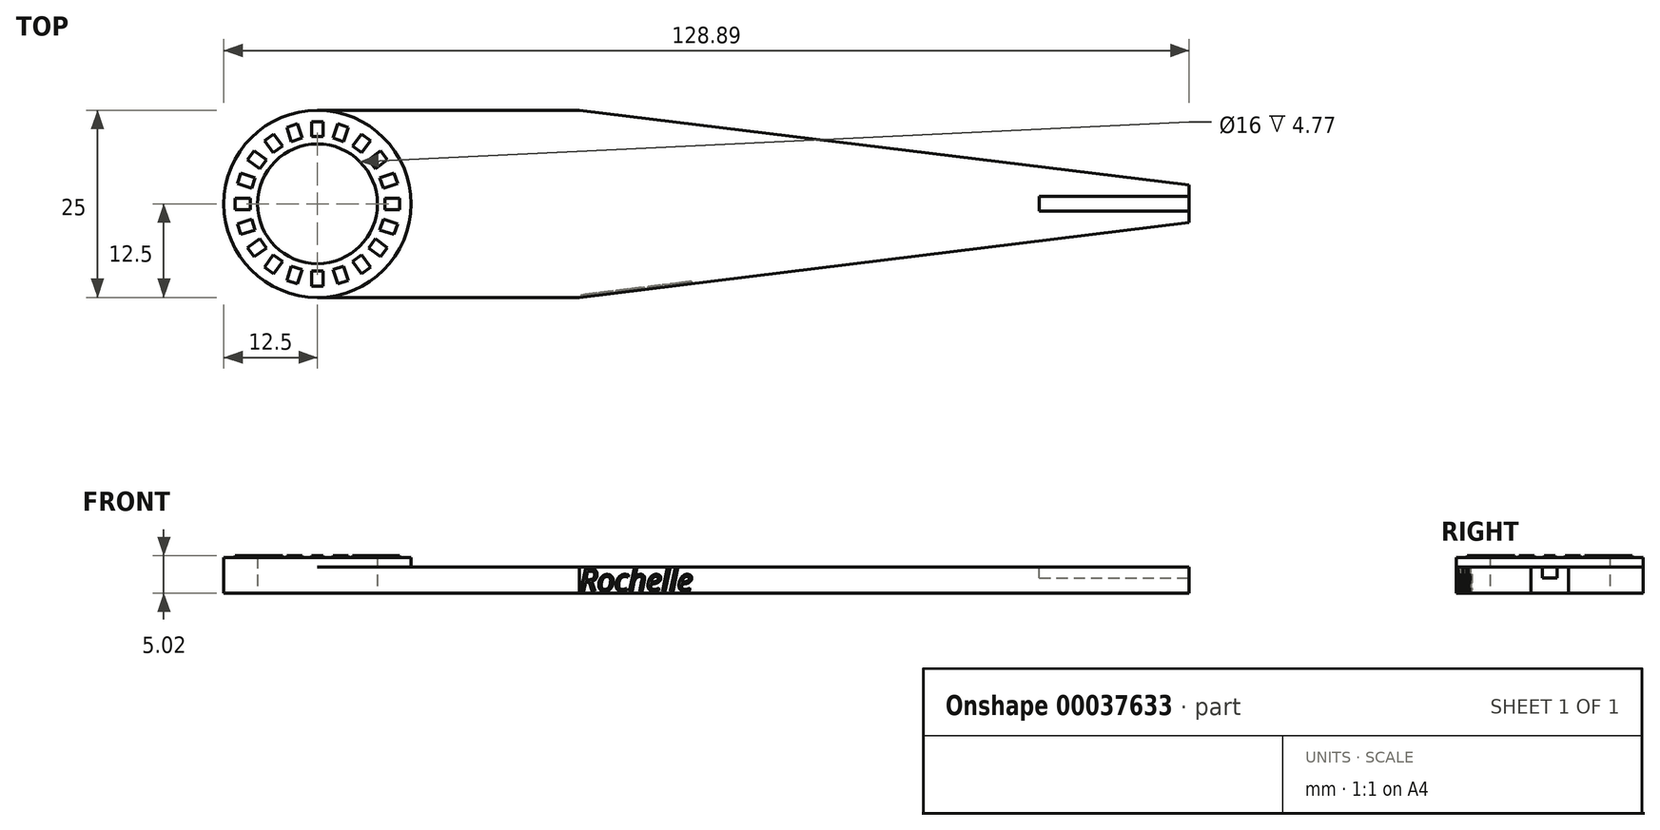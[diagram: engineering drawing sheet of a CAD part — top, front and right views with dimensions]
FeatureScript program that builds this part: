
annotation { "Feature Type Name" : "Feature", "Feature Type Description" : "" }
export const myFeature = defineFeature(function(context is Context, id is Id, definition is map)
    precondition{}
    {
        {
            var Q0;
            Q0=qCreatedBy(makeId("Top.planeOp"),FACE);
            var sketch = newSketch(context, id + "F0", { "sketchPlane" : qUnion([Q0])});
            skCircle(sketch, "E0", {"center": v(0, 0) * mm, "radius": 8 * mm});
            skCircle(sketch, "E1", {"center": v(0, 0) * mm, "radius": 12.5 * mm});
            skLineSegment(sketch, "E2", {"start": v(0, 12.5) * mm, "end": v(35, 12.5) * mm});
            skPoint(sketch, "E3", {"position": v(0, 12.5) * mm});
            skLineSegment(sketch, "E4", {"start": v(0, 0) * mm, "end": v(34.23, 0) * mm, "construction": true});
            skLineSegment(sketch, "E5.MirrorCS", {"start": v(0, -12.5) * mm, "end": v(35, -12.5) * mm});
            skLineSegment(sketch, "E6", {"start": v(35, 12.5) * mm, "end": v(74.55, 12.5) * mm, "construction": true});
            skLineSegment(sketch, "E7", {"start": v(35, 12.5) * mm, "end": v(116.39, 2.5) * mm});
            skLineSegment(sketch, "E8.MirrorCS", {"start": v(35, -12.5) * mm, "end": v(116.39, -2.5) * mm});
            skLineSegment(sketch, "E9", {"start": v(116.39, 2.5) * mm, "end": v(116.39, -2.5) * mm});
            skSolve(sketch);
        }
        {
            var Q0;
            Q0 = qSketchRegion(id + "F0", true);
            extrude(context, id + "F1", {"entities" : qUnion([Q0]), "depth" : 3.5 * mm});
        }
        {
            var Q0;
            Q0=makeQuery(id+"F1.opExtrude","CAP_FACE",FACE,{"disambiguationData":[OSD([sQuery(id+"F0.wireOp",EDGE,"E0"),sQuery(id+"F0.wireOp",EDGE,"E1"),sQuery(id+"F0.wireOp",EDGE,"E2"),sQuery(id+"F0.wireOp",EDGE,"E5.MirrorCS"),sQuery(id+"F0.wireOp",EDGE,"E7"),sQuery(id+"F0.wireOp",EDGE,"E8.MirrorCS"),sQuery(id+"F0.wireOp",EDGE,"E9")])],"isStart":false});
            var sketch = newSketch(context, id + "F2", { "sketchPlane" : qUnion([Q0])});
            skCircle(sketch, "E10", {"center": v(0, 0) * mm, "radius": 12.5 * mm});
            skCircle(sketch, "E11", {"center": v(0, 0) * mm, "radius": 8 * mm});
            skSolve(sketch);
        }
        {
            var Q0;
            Q0=makeQuery(id+"F2.imprint","IMPRINT",FACE,{"disambiguationData":[TD([[makeQuery(id+"F2.imprint","IMPRINT",EDGE,{"derivedFrom":sQuery(id+"F2.wireOp",EDGE,"E11")}),-1.0]])]});
            extrude(context, id + "F3", {"entities" : qUnion([Q0]), "operationType" : NewBodyOperationType.ADD, "depth" : 1.27 * mm});
        }
        {
            var Q0;
            Q0=makeQuery(id+"F3.opExtrude","CAP_FACE",FACE,{"disambiguationData":[OSD([sQuery(id+"F2.wireOp",EDGE,"E10"),sQuery(id+"F2.wireOp",EDGE,"E11")])],"isStart":false});
            var sketch = newSketch(context, id + "F4", { "sketchPlane" : qUnion([Q0])});
            skLineSegment(sketch, "E12.rect.bottom", {"start": v(0.75, 9) * mm, "end": v(-0.75, 9) * mm});
            skLineSegment(sketch, "E12.rect.top", {"start": v(0.75, 11) * mm, "end": v(-0.75, 11) * mm});
            skLineSegment(sketch, "E12.rect.left", {"start": v(0.75, 9) * mm, "end": v(0.75, 11) * mm});
            skLineSegment(sketch, "E12.rect.right", {"start": v(-0.75, 9) * mm, "end": v(-0.75, 11) * mm});
            skPoint(sketch, "E12.rect.middle", {"position": v(0, 10) * mm});
            skPoint(sketch, "E13", {"position": v(0, 8) * mm});
            skLineSegment(sketch, "E14.1.0", {"start": v(-2.69, 10.7) * mm, "end": v(-4.11, 10.23) * mm});
            skLineSegment(sketch, "E14.1.1", {"start": v(-2.07, 8.8) * mm, "end": v(-3.5, 8.33) * mm});
            skLineSegment(sketch, "E14.1.2", {"start": v(-3.5, 8.33) * mm, "end": v(-4.11, 10.23) * mm});
            skLineSegment(sketch, "E14.1.3", {"start": v(-2.07, 8.8) * mm, "end": v(-2.69, 10.7) * mm});
            skLineSegment(sketch, "E14.2.0", {"start": v(-5.86, 9.34) * mm, "end": v(-7.07, 8.46) * mm});
            skLineSegment(sketch, "E14.2.1", {"start": v(-4.68, 7.72) * mm, "end": v(-5.9, 6.84) * mm});
            skLineSegment(sketch, "E14.2.2", {"start": v(-5.9, 6.84) * mm, "end": v(-7.07, 8.46) * mm});
            skLineSegment(sketch, "E14.2.3", {"start": v(-4.68, 7.72) * mm, "end": v(-5.86, 9.34) * mm});
            skLineSegment(sketch, "E14.3.0", {"start": v(-8.46, 7.07) * mm, "end": v(-9.34, 5.86) * mm});
            skLineSegment(sketch, "E14.3.1", {"start": v(-6.84, 5.9) * mm, "end": v(-7.72, 4.68) * mm});
            skLineSegment(sketch, "E14.3.2", {"start": v(-7.72, 4.68) * mm, "end": v(-9.34, 5.86) * mm});
            skLineSegment(sketch, "E14.3.3", {"start": v(-6.84, 5.9) * mm, "end": v(-8.46, 7.07) * mm});
            skLineSegment(sketch, "E14.4.0", {"start": v(-10.23, 4.11) * mm, "end": v(-10.7, 2.69) * mm});
            skLineSegment(sketch, "E14.4.1", {"start": v(-8.33, 3.5) * mm, "end": v(-8.8, 2.07) * mm});
            skLineSegment(sketch, "E14.4.2", {"start": v(-8.8, 2.07) * mm, "end": v(-10.7, 2.69) * mm});
            skLineSegment(sketch, "E14.4.3", {"start": v(-8.33, 3.5) * mm, "end": v(-10.23, 4.11) * mm});
            skLineSegment(sketch, "E14.5.0", {"start": v(-11, 0.75) * mm, "end": v(-11, -0.75) * mm});
            skLineSegment(sketch, "E14.5.1", {"start": v(-9, 0.75) * mm, "end": v(-9, -0.75) * mm});
            skLineSegment(sketch, "E14.5.2", {"start": v(-9, -0.75) * mm, "end": v(-11, -0.75) * mm});
            skLineSegment(sketch, "E14.5.3", {"start": v(-9, 0.75) * mm, "end": v(-11, 0.75) * mm});
            skLineSegment(sketch, "E14.6.0", {"start": v(-10.7, -2.69) * mm, "end": v(-10.23, -4.11) * mm});
            skLineSegment(sketch, "E14.6.1", {"start": v(-8.8, -2.07) * mm, "end": v(-8.33, -3.5) * mm});
            skLineSegment(sketch, "E14.6.2", {"start": v(-8.33, -3.5) * mm, "end": v(-10.23, -4.11) * mm});
            skLineSegment(sketch, "E14.6.3", {"start": v(-8.8, -2.07) * mm, "end": v(-10.7, -2.69) * mm});
            skLineSegment(sketch, "E14.7.0", {"start": v(-9.34, -5.86) * mm, "end": v(-8.46, -7.07) * mm});
            skLineSegment(sketch, "E14.7.1", {"start": v(-7.72, -4.68) * mm, "end": v(-6.84, -5.9) * mm});
            skLineSegment(sketch, "E14.7.2", {"start": v(-6.84, -5.9) * mm, "end": v(-8.46, -7.07) * mm});
            skLineSegment(sketch, "E14.7.3", {"start": v(-7.72, -4.68) * mm, "end": v(-9.34, -5.86) * mm});
            skLineSegment(sketch, "E14.8.0", {"start": v(-7.07, -8.46) * mm, "end": v(-5.86, -9.34) * mm});
            skLineSegment(sketch, "E14.8.1", {"start": v(-5.9, -6.84) * mm, "end": v(-4.68, -7.72) * mm});
            skLineSegment(sketch, "E14.8.2", {"start": v(-4.68, -7.72) * mm, "end": v(-5.86, -9.34) * mm});
            skLineSegment(sketch, "E14.8.3", {"start": v(-5.9, -6.84) * mm, "end": v(-7.07, -8.46) * mm});
            skLineSegment(sketch, "E14.9.0", {"start": v(-4.11, -10.23) * mm, "end": v(-2.69, -10.7) * mm});
            skLineSegment(sketch, "E14.9.1", {"start": v(-3.5, -8.33) * mm, "end": v(-2.07, -8.8) * mm});
            skLineSegment(sketch, "E14.9.2", {"start": v(-2.07, -8.8) * mm, "end": v(-2.69, -10.7) * mm});
            skLineSegment(sketch, "E14.9.3", {"start": v(-3.5, -8.33) * mm, "end": v(-4.11, -10.23) * mm});
            skLineSegment(sketch, "E14.10.0", {"start": v(-0.75, -11) * mm, "end": v(0.75, -11) * mm});
            skLineSegment(sketch, "E14.10.1", {"start": v(-0.75, -9) * mm, "end": v(0.75, -9) * mm});
            skLineSegment(sketch, "E14.10.2", {"start": v(0.75, -9) * mm, "end": v(0.75, -11) * mm});
            skLineSegment(sketch, "E14.10.3", {"start": v(-0.75, -9) * mm, "end": v(-0.75, -11) * mm});
            skLineSegment(sketch, "E14.11.0", {"start": v(2.69, -10.7) * mm, "end": v(4.11, -10.23) * mm});
            skLineSegment(sketch, "E14.11.1", {"start": v(2.07, -8.8) * mm, "end": v(3.5, -8.33) * mm});
            skLineSegment(sketch, "E14.11.2", {"start": v(3.5, -8.33) * mm, "end": v(4.11, -10.23) * mm});
            skLineSegment(sketch, "E14.11.3", {"start": v(2.07, -8.8) * mm, "end": v(2.69, -10.7) * mm});
            skLineSegment(sketch, "E14.12.0", {"start": v(5.86, -9.34) * mm, "end": v(7.07, -8.46) * mm});
            skLineSegment(sketch, "E14.12.1", {"start": v(4.68, -7.72) * mm, "end": v(5.9, -6.84) * mm});
            skLineSegment(sketch, "E14.12.2", {"start": v(5.9, -6.84) * mm, "end": v(7.07, -8.46) * mm});
            skLineSegment(sketch, "E14.12.3", {"start": v(4.68, -7.72) * mm, "end": v(5.86, -9.34) * mm});
            skLineSegment(sketch, "E14.13.0", {"start": v(8.46, -7.07) * mm, "end": v(9.34, -5.86) * mm});
            skLineSegment(sketch, "E14.13.1", {"start": v(6.84, -5.9) * mm, "end": v(7.72, -4.68) * mm});
            skLineSegment(sketch, "E14.13.2", {"start": v(7.72, -4.68) * mm, "end": v(9.34, -5.86) * mm});
            skLineSegment(sketch, "E14.13.3", {"start": v(6.84, -5.9) * mm, "end": v(8.46, -7.07) * mm});
            skLineSegment(sketch, "E14.14.0", {"start": v(10.23, -4.11) * mm, "end": v(10.7, -2.69) * mm});
            skLineSegment(sketch, "E14.14.1", {"start": v(8.33, -3.5) * mm, "end": v(8.8, -2.07) * mm});
            skLineSegment(sketch, "E14.14.2", {"start": v(8.8, -2.07) * mm, "end": v(10.7, -2.69) * mm});
            skLineSegment(sketch, "E14.14.3", {"start": v(8.33, -3.5) * mm, "end": v(10.23, -4.11) * mm});
            skLineSegment(sketch, "E14.15.0", {"start": v(11, -0.75) * mm, "end": v(11, 0.75) * mm});
            skLineSegment(sketch, "E14.15.1", {"start": v(9, -0.75) * mm, "end": v(9, 0.75) * mm});
            skLineSegment(sketch, "E14.15.2", {"start": v(9, 0.75) * mm, "end": v(11, 0.75) * mm});
            skLineSegment(sketch, "E14.15.3", {"start": v(9, -0.75) * mm, "end": v(11, -0.75) * mm});
            skLineSegment(sketch, "E14.16.0", {"start": v(10.7, 2.69) * mm, "end": v(10.23, 4.11) * mm});
            skLineSegment(sketch, "E14.16.1", {"start": v(8.8, 2.07) * mm, "end": v(8.33, 3.5) * mm});
            skLineSegment(sketch, "E14.16.2", {"start": v(8.33, 3.5) * mm, "end": v(10.23, 4.11) * mm});
            skLineSegment(sketch, "E14.16.3", {"start": v(8.8, 2.07) * mm, "end": v(10.7, 2.69) * mm});
            skLineSegment(sketch, "E14.17.0", {"start": v(9.34, 5.86) * mm, "end": v(8.46, 7.07) * mm});
            skLineSegment(sketch, "E14.17.1", {"start": v(7.72, 4.68) * mm, "end": v(6.84, 5.9) * mm});
            skLineSegment(sketch, "E14.17.2", {"start": v(6.84, 5.9) * mm, "end": v(8.46, 7.07) * mm});
            skLineSegment(sketch, "E14.17.3", {"start": v(7.72, 4.68) * mm, "end": v(9.34, 5.86) * mm});
            skLineSegment(sketch, "E14.18.0", {"start": v(7.07, 8.46) * mm, "end": v(5.86, 9.34) * mm});
            skLineSegment(sketch, "E14.18.1", {"start": v(5.9, 6.84) * mm, "end": v(4.68, 7.72) * mm});
            skLineSegment(sketch, "E14.18.2", {"start": v(4.68, 7.72) * mm, "end": v(5.86, 9.34) * mm});
            skLineSegment(sketch, "E14.18.3", {"start": v(5.9, 6.84) * mm, "end": v(7.07, 8.46) * mm});
            skLineSegment(sketch, "E14.19.0", {"start": v(4.11, 10.23) * mm, "end": v(2.69, 10.7) * mm});
            skLineSegment(sketch, "E14.19.1", {"start": v(3.5, 8.33) * mm, "end": v(2.07, 8.8) * mm});
            skLineSegment(sketch, "E14.19.2", {"start": v(2.07, 8.8) * mm, "end": v(2.69, 10.7) * mm});
            skLineSegment(sketch, "E14.19.3", {"start": v(3.5, 8.33) * mm, "end": v(4.11, 10.23) * mm});
            skPoint(sketch, "E14.center", {"position": v(0, 0) * mm});
            skSolve(sketch);
        }
        {
            var Q0;
            Q0 = qSketchRegion(id + "F4", true);
            extrude(context, id + "F5", {"entities" : qUnion([Q0]), "operationType" : NewBodyOperationType.ADD, "depth" : .25 * mm});
        }
        {
            var Q0;
            {var subQ2=makeQuery(id+"F1.opExtrude","CAP_EDGE",EDGE,{"disambiguationData":[OSD([sQuery(id+"F0.wireOp",EDGE,"E2")])],"isStart":false});Q0=makeQuery(id+"F2.imprint","IMPRINT",FACE,{"disambiguationData":[TD([[makeQuery(id+"F2.imprint","IMPRINT",EDGE,{"derivedFrom":subQ2}),-1.0]])]});}
            var sketch = newSketch(context, id + "F6", { "sketchPlane" : qUnion([Q0])});
            skLineSegment(sketch, "E15.bottom", {"start": v(96.39, 1) * mm, "end": v(116.39, 1) * mm});
            skLineSegment(sketch, "E15.top", {"start": v(96.39, -1) * mm, "end": v(116.39, -1) * mm});
            skLineSegment(sketch, "E15.left", {"start": v(96.39, 1) * mm, "end": v(96.39, -1) * mm});
            skLineSegment(sketch, "E15.right", {"start": v(116.39, 1) * mm, "end": v(116.39, -1) * mm});
            skPoint(sketch, "E16", {"position": v(116.39, 0) * mm});
            skSolve(sketch);
        }
        {
            var Q0;
            Q0 = qSketchRegion(id + "F6", true);
            extrude(context, id + "F7", {"entities" : qUnion([Q0]), "operationType" : NewBodyOperationType.REMOVE, "oppositeDirection" : true, "depth" : 1.5 * mm});
        }
        {
            var Q0;
            Q0=makeQuery(id+"F1.opExtrude","SWEPT_FACE",FACE,{"disambiguationData":[OSD([sQuery(id+"F0.wireOp",EDGE,"E8.MirrorCS")])]});
            var sketch = newSketch(context, id + "F8", { "sketchPlane" : qUnion([Q0])});
            skText(sketch, "E17", { "text": "Rochelle", "fontName": "OpenSans-Italic.ttf"});
            skPoint(sketch, "E18", {"position": v(33.22, 1.75) * mm});
            const initialGuessF8  = {"E17": [0.03322, 0.00025, 1, 0, 0.003]};
            skSetInitialGuess(sketch, initialGuessF8);
            skSolve(sketch);
        }
        {
            var Q0;
            Q0 = qSketchRegion(id + "F8", true);
            extrude(context, id + "F9", {"entities" : qUnion([Q0]), "operationType" : NewBodyOperationType.REMOVE, "oppositeDirection" : true, "depth" : .3 * mm});
        }
    });
